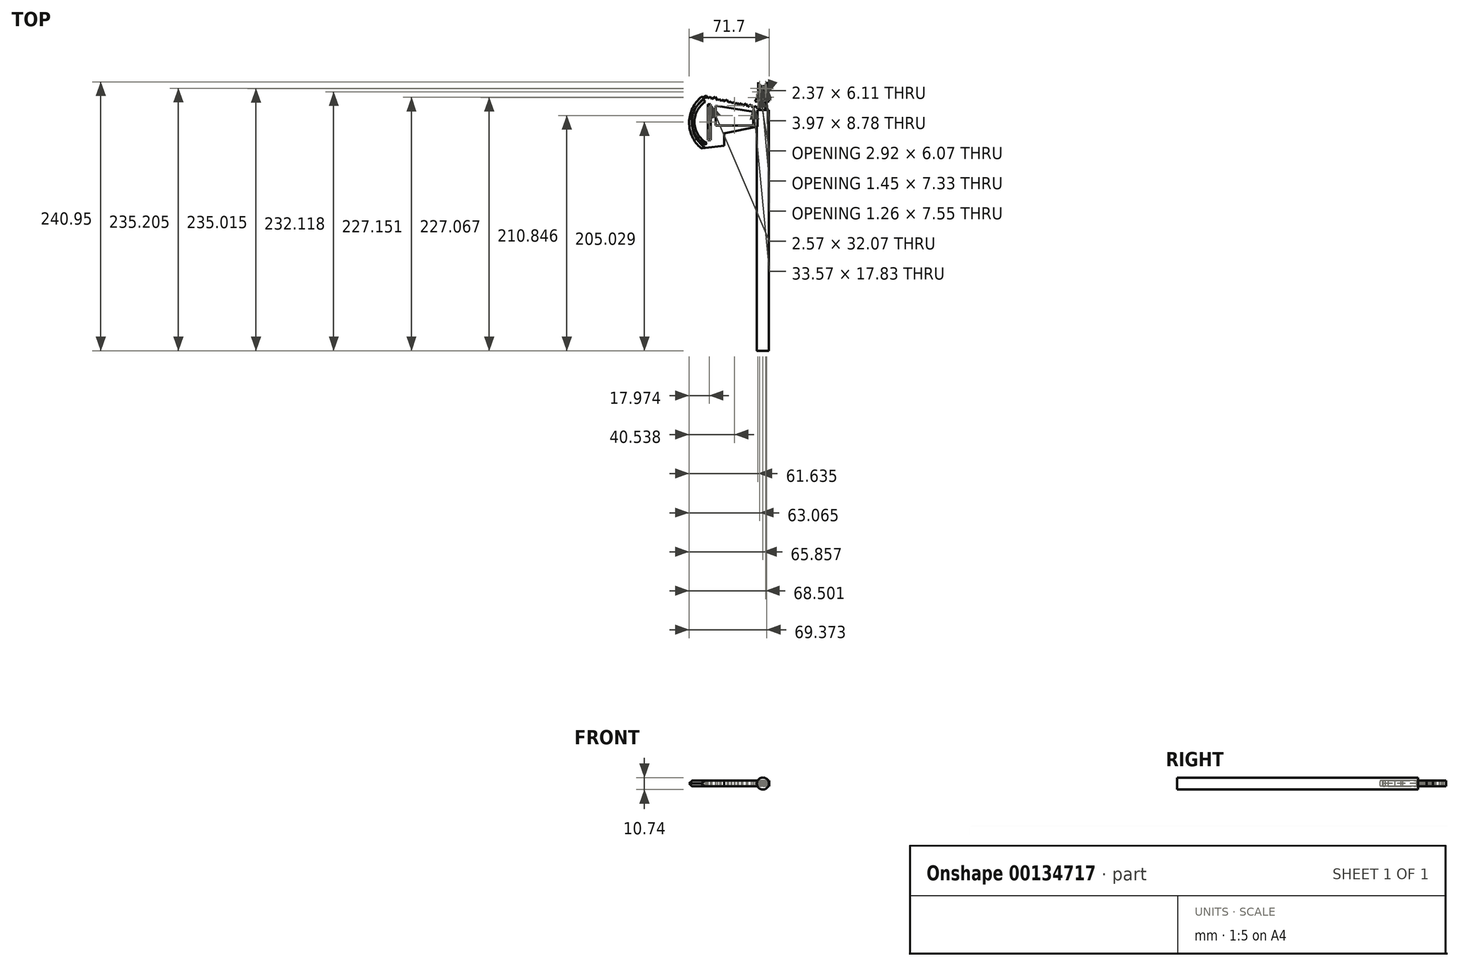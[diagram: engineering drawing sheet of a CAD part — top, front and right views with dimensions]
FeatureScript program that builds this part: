
annotation { "Feature Type Name" : "Feature", "Feature Type Description" : "" }
export const myFeature = defineFeature(function(context is Context, id is Id, definition is map)
    precondition{}
    {
        {
            var Q0;
            Q0=qCreatedBy(makeId("Front.planeOp"),FACE);
            var sketch = newSketch(context, id + "F0", { "sketchPlane" : qUnion([Q0])});
            skCircle(sketch, "E0", {"center": v(0, 0) * mm, "radius": 5.37 * mm});
            skSolve(sketch);
        }
        {
            var Q0;
            Q0 = qSketchRegion(id + "F0", true);
            extrude(context, id + "F1", {"entities" : qUnion([Q0]), "depth" : 215.89 * mm});
        }
        {
            var Q0;
            Q0=qCreatedBy(makeId("Top.planeOp"),FACE);
            var sketch = newSketch(context, id + "F2", { "sketchPlane" : qUnion([Q0])});
            skLineSegment(sketch, "E1", {"start": v(-34.75, -21) * mm, "end": v(-34.75, -32.08) * mm});
            skLineSegment(sketch, "E2", {"start": v(-34.75, -32.08) * mm, "end": v(-55.37, -34.32) * mm});
            skLineSegment(sketch, "E3", {"start": v(-34.75, -21) * mm, "end": v(0, -14.1) * mm});
            skLineSegment(sketch, "E4", {"start": v(0, -14.1) * mm, "end": v(0, 0) * mm});
            skLineSegment(sketch, "E5", {"start": v(0, 0) * mm, "end": v(0, 0) * mm});
            skLineSegment(sketch, "E6", {"start": v(0, 0) * mm, "end": v(-55, 11.69) * mm});
            skArc(sketch, "E7", {"start": v(-55, 11.69) * mm, "mid": v(-66.07, -11.23) * mm, "end": v(-55.37, -34.32) * mm});
            skLineSegment(sketch, "E8", {"start": v(2.17, 0) * mm, "end": v(2.17, 7.62) * mm});
            skLineSegment(sketch, "E9", {"start": v(5.62, 7.67) * mm, "end": v(0, 22.08) * mm});
            skLineSegment(sketch, "E10", {"start": v(0, 22.08) * mm, "end": v(-6.95, 7.62) * mm});
            skLineSegment(sketch, "E11", {"start": v(-2.95, 0) * mm, "end": v(-2.95, 7.62) * mm});
            skLineSegment(sketch, "E12", {"start": v(-6.95, 7.62) * mm, "end": v(-2.95, 7.62) * mm});
            skLineSegment(sketch, "E13", {"start": v(2.17, 7.62) * mm, "end": v(5.62, 7.67) * mm});
            skLineSegment(sketch, "E14", {"start": v(-4.23, 13.29) * mm, "end": v(-4.23, 24.84) * mm});
            skLineSegment(sketch, "E15", {"start": v(-4.23, 24.84) * mm, "end": v(-1.42, 19.13) * mm});
            skLineSegment(sketch, "E16", {"start": v(1.2, 19) * mm, "end": v(3.36, 25.06) * mm});
            skLineSegment(sketch, "E17", {"start": v(3.36, 25.06) * mm, "end": v(3.36, 13.45) * mm});
            skLineSegment(sketch, "E18", {"start": v(-2.95, 0) * mm, "end": v(2.17, 0) * mm});
            skLineSegment(sketch, "E19", {"start": v(4.48, 8.24) * mm, "end": v(2.17, 8.2) * mm});
            skLineSegment(sketch, "E20", {"start": v(2.17, 8.2) * mm, "end": v(2.1, 13.02) * mm});
            skLineSegment(sketch, "E21", {"start": v(-2.99, 8.14) * mm, "end": v(-2.99, 13.02) * mm});
            skLineSegment(sketch, "E22", {"start": v(-2.99, 8.14) * mm, "end": v(-5.9, 8.14) * mm});
            skLineSegment(sketch, "E23", {"start": v(-5.9, 8.14) * mm, "end": v(-2.99, 14.21) * mm});
            skLineSegment(sketch, "E24", {"start": v(-2.99, 14.21) * mm, "end": v(-2.99, 13.02) * mm});
            skLineSegment(sketch, "E25", {"start": v(4.48, 8.24) * mm, "end": v(2.1, 14.31) * mm});
            skLineSegment(sketch, "E26", {"start": v(2.1, 14.31) * mm, "end": v(2.1, 13.02) * mm});
            skLineSegment(sketch, "E27", {"start": v(-2.29, 19.1) * mm, "end": v(-3.74, 15.65) * mm});
            skLineSegment(sketch, "E28", {"start": v(-3.74, 15.65) * mm, "end": v(-3.74, 22.98) * mm});
            skLineSegment(sketch, "E29", {"start": v(-3.74, 22.98) * mm, "end": v(-2.29, 19.1) * mm});
            skLineSegment(sketch, "E30", {"start": v(3.05, 15.35) * mm, "end": v(3.05, 22.9) * mm});
            skLineSegment(sketch, "E31", {"start": v(3.05, 22.9) * mm, "end": v(1.8, 18.93) * mm});
            skLineSegment(sketch, "E32", {"start": v(1.8, 18.93) * mm, "end": v(3.05, 15.35) * mm});
            skLineSegment(sketch, "E33", {"start": v(0, 20.62) * mm, "end": v(-2.21, 15.92) * mm});
            skLineSegment(sketch, "E34", {"start": v(-2.21, 15.92) * mm, "end": v(0, 11.84) * mm});
            skLineSegment(sketch, "E35", {"start": v(0, 11.84) * mm, "end": v(1.76, 16) * mm});
            skLineSegment(sketch, "E36", {"start": v(1.76, 16) * mm, "end": v(0, 20.62) * mm});
            skArc(sketch, "E37", {"start": v(-53.18, 9.23) * mm, "mid": v(-63.62, -11.49) * mm, "end": v(-51.42, -31.23) * mm});
            skLineSegment(sketch, "E38", {"start": v(-51.42, -31.23) * mm, "end": v(-50.34, -29.6) * mm});
            skLineSegment(sketch, "E39", {"start": v(-53.18, 9.23) * mm, "end": v(-51.54, 7.3) * mm});
            skArc(sketch, "E40", {"start": v(-51.54, 7.3) * mm, "mid": v(-61.36, -11.5) * mm, "end": v(-50.34, -29.6) * mm});
            skLineSegment(sketch, "E41", {"start": v(-49.26, 5.17) * mm, "end": v(-46.82, 5.17) * mm});
            skLineSegment(sketch, "E42", {"start": v(-46.82, 5.17) * mm, "end": v(-46.82, -26.9) * mm});
            skLineSegment(sketch, "E43", {"start": v(-46.82, -26.9) * mm, "end": v(-49.4, -26.9) * mm});
            skLineSegment(sketch, "E44", {"start": v(-49.4, -26.9) * mm, "end": v(-49.26, 5.17) * mm});
            skLineSegment(sketch, "E45", {"start": v(-45.8, 9.73) * mm, "end": v(-42.72, 11.69) * mm});
            skLineSegment(sketch, "E46", {"start": v(-42.72, 11.69) * mm, "end": v(-40.8, 8.67) * mm});
            skLineSegment(sketch, "E47", {"start": v(-40.8, 8.67) * mm, "end": v(-38.85, 9.9) * mm});
            skLineSegment(sketch, "E48", {"start": v(-38.85, 9.9) * mm, "end": v(-37.64, 8) * mm});
            skLineSegment(sketch, "E49", {"start": v(-37.64, 8) * mm, "end": v(-35.2, 9.55) * mm});
            skLineSegment(sketch, "E50", {"start": v(-35.2, 9.55) * mm, "end": v(-35.2, 7.48) * mm});
            skLineSegment(sketch, "E51", {"start": v(-35.2, 7.48) * mm, "end": v(-32.15, 9.12) * mm});
            skLineSegment(sketch, "E52", {"start": v(-32.15, 9.12) * mm, "end": v(-30.75, 6.53) * mm});
            skLineSegment(sketch, "E53", {"start": v(-30.75, 6.53) * mm, "end": v(-28.79, 7.6) * mm});
            skLineSegment(sketch, "E54", {"start": v(-28.79, 7.6) * mm, "end": v(-27.9, 5.93) * mm});
            skLineSegment(sketch, "E55", {"start": v(-27.9, 5.93) * mm, "end": v(-25.93, 6.98) * mm});
            skLineSegment(sketch, "E56", {"start": v(-25.93, 6.98) * mm, "end": v(-25.04, 5.32) * mm});
            skLineSegment(sketch, "E57", {"start": v(-25.04, 5.32) * mm, "end": v(-22.97, 6.44) * mm});
            skLineSegment(sketch, "E58", {"start": v(-22.97, 6.44) * mm, "end": v(-22.02, 4.68) * mm});
            skLineSegment(sketch, "E59", {"start": v(-22.02, 4.68) * mm, "end": v(-19.45, 6.06) * mm});
            skLineSegment(sketch, "E60", {"start": v(-19.45, 6.06) * mm, "end": v(-18.27, 3.88) * mm});
            skLineSegment(sketch, "E61", {"start": v(-18.27, 3.88) * mm, "end": v(-15.15, 5.57) * mm});
            skLineSegment(sketch, "E62", {"start": v(-15.15, 5.57) * mm, "end": v(-13.72, 2.92) * mm});
            skLineSegment(sketch, "E63", {"start": v(-13.72, 2.92) * mm, "end": v(-10.45, 4.68) * mm});
            skLineSegment(sketch, "E64", {"start": v(-10.45, 4.68) * mm, "end": v(-8.95, 1.9) * mm});
            skLineSegment(sketch, "E65", {"start": v(-8.95, 1.9) * mm, "end": v(-6.16, 3.4) * mm});
            skLineSegment(sketch, "E66", {"start": v(-6.16, 3.4) * mm, "end": v(-4.88, 1.04) * mm});
            skLineSegment(sketch, "E67", {"start": v(-45.8, 9.73) * mm, "end": v(-47.13, 11.83) * mm});
            skLineSegment(sketch, "E68", {"start": v(-47.13, 11.83) * mm, "end": v(-49.28, 10.47) * mm});
            skLineSegment(sketch, "E69", {"start": v(-49.28, 10.47) * mm, "end": v(-50.85, 12.95) * mm});
            skLineSegment(sketch, "E70", {"start": v(-50.85, 12.95) * mm, "end": v(-53.39, 11.34) * mm});
            skLineSegment(sketch, "E71.bottom", {"start": v(-8.76, -1.54) * mm, "end": v(-42.33, -1.54) * mm});
            skLineSegment(sketch, "E71.top", {"start": v(-8.76, -13.96) * mm, "end": v(-42.33, -13.96) * mm});
            skLineSegment(sketch, "E71.left", {"start": v(-8.76, -1.54) * mm, "end": v(-8.76, -13.96) * mm});
            skLineSegment(sketch, "E71.right", {"start": v(-42.33, -1.54) * mm, "end": v(-42.33, -13.96) * mm});
            skLineSegment(sketch, "E72", {"start": v(-42.33, -1.54) * mm, "end": v(-42.33, 3.87) * mm});
            skLineSegment(sketch, "E73", {"start": v(-42.33, 3.87) * mm, "end": v(-8.76, -1.54) * mm});
            skSolve(sketch);
        }
        {
            var Q0;
            {var subQ0=sQuery(id+"F2.wireOp",EDGE,"E65");Q0=makeQuery(id+"F2.imprint","IMPRINT",FACE,{"disambiguationData":[TD([[makeQuery(id+"F2.imprint","IMPRINT",EDGE,{"derivedFrom":subQ0}),-1.0]])]});}
            var Q1;
            {var subQ0=sQuery(id+"F2.wireOp",EDGE,"E63");Q1=makeQuery(id+"F2.imprint","IMPRINT",FACE,{"disambiguationData":[TD([[makeQuery(id+"F2.imprint","IMPRINT",EDGE,{"derivedFrom":subQ0}),-1.0]])]});}
            var Q2;
            {var subQ0=sQuery(id+"F2.wireOp",EDGE,"E61");Q2=makeQuery(id+"F2.imprint","IMPRINT",FACE,{"disambiguationData":[TD([[makeQuery(id+"F2.imprint","IMPRINT",EDGE,{"derivedFrom":subQ0}),-1.0]])]});}
            var Q3;
            {var subQ0=sQuery(id+"F2.wireOp",EDGE,"E59");Q3=makeQuery(id+"F2.imprint","IMPRINT",FACE,{"disambiguationData":[TD([[makeQuery(id+"F2.imprint","IMPRINT",EDGE,{"derivedFrom":subQ0}),-1.0]])]});}
            var Q4;
            {var subQ0=sQuery(id+"F2.wireOp",EDGE,"E57");Q4=makeQuery(id+"F2.imprint","IMPRINT",FACE,{"disambiguationData":[TD([[makeQuery(id+"F2.imprint","IMPRINT",EDGE,{"derivedFrom":subQ0}),-1.0]])]});}
            var Q5;
            {var subQ0=sQuery(id+"F2.wireOp",EDGE,"E55");Q5=makeQuery(id+"F2.imprint","IMPRINT",FACE,{"disambiguationData":[TD([[makeQuery(id+"F2.imprint","IMPRINT",EDGE,{"derivedFrom":subQ0}),-1.0]])]});}
            var Q6;
            {var subQ0=sQuery(id+"F2.wireOp",EDGE,"E53");Q6=makeQuery(id+"F2.imprint","IMPRINT",FACE,{"disambiguationData":[TD([[makeQuery(id+"F2.imprint","IMPRINT",EDGE,{"derivedFrom":subQ0}),-1.0]])]});}
            var Q7;
            {var subQ0=sQuery(id+"F2.wireOp",EDGE,"E51");Q7=makeQuery(id+"F2.imprint","IMPRINT",FACE,{"disambiguationData":[TD([[makeQuery(id+"F2.imprint","IMPRINT",EDGE,{"derivedFrom":subQ0}),-1.0]])]});}
            var Q8;
            {var subQ0=sQuery(id+"F2.wireOp",EDGE,"E49");Q8=makeQuery(id+"F2.imprint","IMPRINT",FACE,{"disambiguationData":[TD([[makeQuery(id+"F2.imprint","IMPRINT",EDGE,{"derivedFrom":subQ0}),-1.0]])]});}
            var Q9;
            {var subQ0=sQuery(id+"F2.wireOp",EDGE,"E47");Q9=makeQuery(id+"F2.imprint","IMPRINT",FACE,{"disambiguationData":[TD([[makeQuery(id+"F2.imprint","IMPRINT",EDGE,{"derivedFrom":subQ0}),-1.0]])]});}
            var Q10;
            {var subQ0=sQuery(id+"F2.wireOp",EDGE,"E45");Q10=makeQuery(id+"F2.imprint","IMPRINT",FACE,{"disambiguationData":[TD([[makeQuery(id+"F2.imprint","IMPRINT",EDGE,{"derivedFrom":subQ0}),-1.0]])]});}
            var Q11;
            {var subQ0=sQuery(id+"F2.wireOp",EDGE,"E67");Q11=makeQuery(id+"F2.imprint","IMPRINT",FACE,{"disambiguationData":[TD([[makeQuery(id+"F2.imprint","IMPRINT",EDGE,{"derivedFrom":subQ0}),1.0]])]});}
            var Q12;
            {var subQ0=sQuery(id+"F2.wireOp",EDGE,"E69");Q12=makeQuery(id+"F2.imprint","IMPRINT",FACE,{"disambiguationData":[TD([[makeQuery(id+"F2.imprint","IMPRINT",EDGE,{"derivedFrom":subQ0}),1.0]])]});}
            var Q13;
            {var subQ0=sQuery(id+"F2.wireOp",EDGE,"E18");var subQ3=sQuery(id+"F2.wireOp",EDGE,"E11");var subQ5=makeQuery(id+"F2.imprint","INTERSECT",VERTEX,{"derivedFrom":[subQ3,subQ0]});Q13=makeQuery(id+"F2.imprint","IMPRINT",FACE,{"disambiguationData":[TD([[makeQuery(id+"F2.imprint","IMPRINT",EDGE,{"disambiguationData":[TD([[subQ5,-1.0]])],"derivedFrom":subQ3}),-1.0]])]});}
            var Q14;
            {var subQ1=sQuery(id+"F2.wireOp",EDGE,"E16");Q14=makeQuery(id+"F2.imprint","IMPRINT",FACE,{"disambiguationData":[TD([[makeQuery(id+"F2.imprint","IMPRINT",EDGE,{"derivedFrom":subQ1}),-1.0]])]});}
            var Q15;
            {var subQ1=sQuery(id+"F2.wireOp",EDGE,"E14");Q15=makeQuery(id+"F2.imprint","IMPRINT",FACE,{"disambiguationData":[TD([[makeQuery(id+"F2.imprint","IMPRINT",EDGE,{"derivedFrom":subQ1}),-1.0]])]});}
            var Q16;
            {var subQ5=sQuery(id+"F2.wireOp",EDGE,"E8");Q16=makeQuery(id+"F2.imprint","IMPRINT",FACE,{"disambiguationData":[TD([[makeQuery(id+"F2.imprint","IMPRINT",EDGE,{"derivedFrom":subQ5}),1.0]])]});}
            var Q17;
            Q17=makeQuery(id+"F2.imprint","IMPRINT",FACE,{"disambiguationData":[TD([[makeQuery(id+"F2.imprint","IMPRINT",EDGE,{"derivedFrom":sQuery(id+"F2.wireOp",EDGE,"E1")}),-1.0]])]});
            extrude(context, id + "F3", {"entities" : qUnion([Q0, Q1, Q2, Q3, Q4, Q5, Q6, Q7, Q8, Q9, Q10, Q11, Q12, Q13, Q14, Q15, Q16, Q17]), "operationType" : NewBodyOperationType.ADD, "depth" : 2.54 * mm, "hasSecondDirection" : true, "secondDirectionOppositeDirection" : true, "secondDirectionDepth" : 2.54 * mm});
        }
        {
            var Q0;
            Q0=makeQuery(id+"F3.opExtrude","CAP_EDGE",EDGE,{"disambiguationData":[OSD([sQuery(id+"F2.wireOp",EDGE,"E7")])],"isStart":false});
            var Q1;
            Q1=makeQuery(id+"F3.opExtrude","CAP_EDGE",EDGE,{"disambiguationData":[OSD([sQuery(id+"F2.wireOp",EDGE,"E7")])],"isStart":true});
            chamfer(context, id + "F4", {"entities" : qUnion([Q0, Q1]), "width" : 2.54 * mm, "tangentPropagation" : true});
        }
    });
